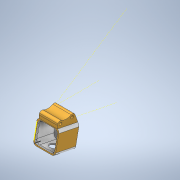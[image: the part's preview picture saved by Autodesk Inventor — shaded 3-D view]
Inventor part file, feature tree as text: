
AUTODESK INVENTOR PART (.ipt)
format: ipt  version: 2020 (Build 240168000, 168)  size: 251,392 bytes
history: native  units: mm
features: other x3, sketch x3, projected_geometry x2, extrude x1
ambient origin geometry x8: Origin, YZ Plane, XZ Plane, XY Plane, X Axis, Y Axis, Z Axis, Center Point
bodies: Solid1 (feature_tree)
feature tree (9):
  other  "V2 modular session template.iam"
  other  "V2 modular session camera case.ipt:1"
  other  "V2 modular session frame mount.ipt:1"
  extrude  "Extrusion1"  Depth=10.0mm TaperAngle=0.0deg
  sketch  "Sketch6"
  sketch  "Sketch7"
  sketch  "Sketch3"  dims[d0=10.0mm d1=10.0mm d2=0.0mm]
  projected_geometry  "Projected Loop1"
  projected_geometry  "Projected Loop2"
